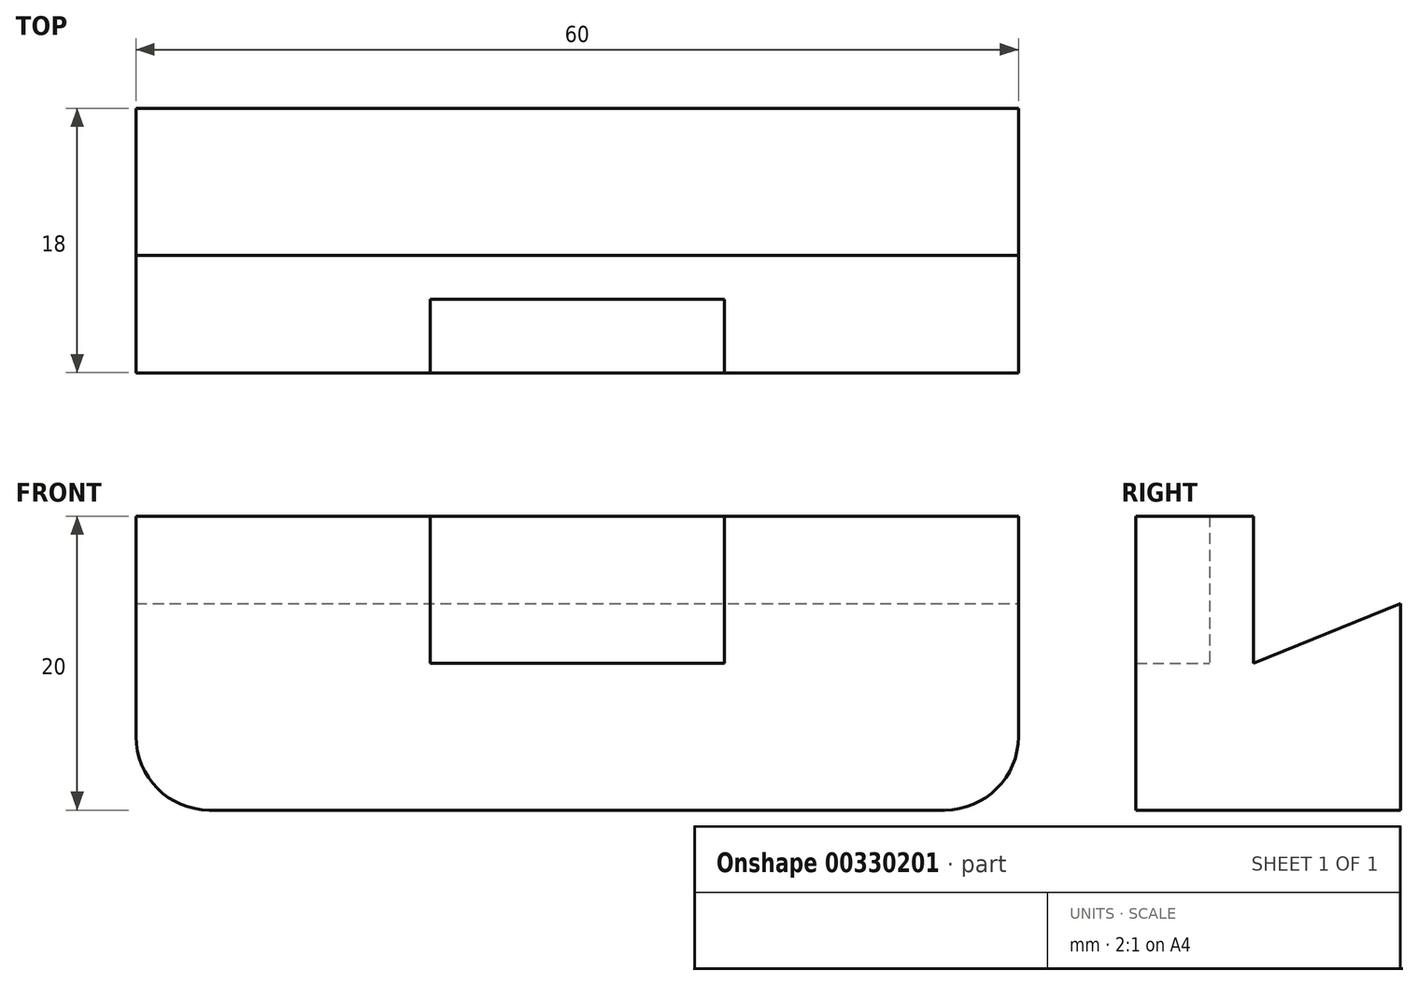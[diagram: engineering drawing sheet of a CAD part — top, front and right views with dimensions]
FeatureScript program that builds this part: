
annotation { "Feature Type Name" : "Feature", "Feature Type Description" : "" }
export const myFeature = defineFeature(function(context is Context, id is Id, definition is map)
    precondition{}
    {
        {
            var Q0;
            Q0=qCreatedBy(makeId("Top.planeOp"),FACE);
            var sketch = newSketch(context, id + "F0", { "sketchPlane" : qUnion([Q0])});
            skLineSegment(sketch, "E0.top", {"start": v(17.49, -21.5) * mm, "end": v(37.49, -21.5) * mm});
            skLineSegment(sketch, "E0.right", {"start": v(37.49, -13.5) * mm, "end": v(37.49, -21.5) * mm});
            skLineSegment(sketch, "E1", {"start": v(17.49, -16.5) * mm, "end": v(17.49, -21.5) * mm});
            skLineSegment(sketch, "E2.MirrorCS", {"start": v(-2.51, -16.5) * mm, "end": v(-2.51, -21.5) * mm});
            skLineSegment(sketch, "E3.MirrorCS", {"start": v(-2.51, -21.5) * mm, "end": v(-22.51, -21.5) * mm});
            skLineSegment(sketch, "E4.MirrorCS", {"start": v(-22.51, -13.5) * mm, "end": v(-22.51, -21.5) * mm});
            skLineSegment(sketch, "E5", {"start": v(-2.51, -16.5) * mm, "end": v(17.49, -16.5) * mm});
            skLineSegment(sketch, "E6", {"start": v(37.49, -13.5) * mm, "end": v(-22.51, -13.5) * mm});
            skPoint(sketch, "E7.startSnap0", {"position": v(7.49, -16.5) * mm});
            skPoint(sketch, "E7.endSnap0", {"position": v(7.49, -13.5) * mm});
            skSolve(sketch);
        }
        {
            var Q0;
            Q0=qSketchRegion(id+"F0",true);
            extrude(context, id + "F1", {"entities" : qUnion([Q0]), "depth" : 20 * mm});
        }
        {
            var Q0;
            Q0=makeQuery(id+"F1.opExtrude","CAP_EDGE",EDGE,{"disambiguationData":[OSD([sQuery(id+"F0.wireOp",EDGE,"E4.MirrorCS")])],"isStart":true});
            var Q1;
            Q1=makeQuery(id+"F1.opExtrude","CAP_EDGE",EDGE,{"disambiguationData":[OSD([sQuery(id+"F0.wireOp",EDGE,"E0.right")])],"isStart":true});
            fillet(context, id + "F2", {"entities" : qUnion([Q0, Q1]), "radius" : 5 * mm, "tangentPropagation" : true, "allowEdgeOverflow" : false});
        }
        {
            var Q0;
            Q0=makeQuery(id+"F1.opExtrude","SWEPT_FACE",FACE,{"disambiguationData":[OSD([sQuery(id+"F0.wireOp",EDGE,"E5")])]});
            var sketch = newSketch(context, id + "F3", { "sketchPlane" : qUnion([Q0])});
            skLineSegment(sketch, "E8.bottom", {"start": v(-2.51, 10) * mm, "end": v(17.49, 10) * mm});
            skLineSegment(sketch, "E8.top", {"start": v(-2.51, 0) * mm, "end": v(17.49, 0) * mm});
            skLineSegment(sketch, "E8.left", {"start": v(-2.51, 10) * mm, "end": v(-2.51, 0) * mm});
            skLineSegment(sketch, "E8.right", {"start": v(17.49, 10) * mm, "end": v(17.49, 0) * mm});
            skSolve(sketch);
        }
        {
            var Q0;
            Q0=makeQuery(id+"F3.imprint","IMPRINT",FACE,{"disambiguationData":[TD([[makeQuery(id+"F3.imprint","IMPRINT",EDGE,{"derivedFrom":sQuery(id+"F3.wireOp",EDGE,"E8.bottom")}),-1.0]])]});
            var Q1;
            Q1 = qSketchRegion(id + "F3", true);
            extrude(context, id + "F4", {"entities" : qUnion([Q0, Q1]), "operationType" : NewBodyOperationType.ADD, "depth" : 5 * mm});
        }
        {
            var Q0;
            Q0=makeQuery(id+"F1.opExtrude","SWEPT_FACE",FACE,{"disambiguationData":[OSD([sQuery(id+"F0.wireOp",EDGE,"E6")])]});
            extrude(context, id + "F5", {"entities" : qUnion([Q0]), "operationType" : NewBodyOperationType.ADD, "depth" : 10 * mm});
        }
        {
            var Q0;
            {var subQ0=sQuery(id+"F0.wireOp",EDGE,"E6");var subQ1=sQuery(id+"F0.wireOp",EDGE,"E0.right");Q0=makeQuery(id+"F5.boolean.opBoolean","MERGE",FACE,{"derivedFrom":[makeQuery(id+"F1.opExtrude","SWEPT_FACE",FACE,{"disambiguationData":[OSD([subQ1])]}),makeQuery(id+"F5.opExtrude","SWEPT_FACE",FACE,{"disambiguationData":[OSD([subQ1,subQ0]),TDD([makeQuery(id+"F1.opExtrude","SWEPT_EDGE",EDGE,{"disambiguationData":[OSD([subQ1,subQ0])]})])]})]});}
            var sketch = newSketch(context, id + "F6", { "sketchPlane" : qUnion([Q0])});
            skLineSegment(sketch, "E9.bottom", {"start": v(-3.5, 20) * mm, "end": v(-13.5, 20) * mm});
            skLineSegment(sketch, "E9.top", {"start": v(-3.5, 14.04) * mm, "end": v(-13.5, 10) * mm});
            skLineSegment(sketch, "E9.left", {"start": v(-3.5, 20) * mm, "end": v(-3.5, 14.04) * mm});
            skLineSegment(sketch, "E9.right", {"start": v(-13.5, 20) * mm, "end": v(-13.5, 10) * mm});
            skSolve(sketch);
        }
        {
            var Q0;
            Q0=makeQuery(id+"F6.imprint","IMPRINT",FACE,{"disambiguationData":[TD([[makeQuery(id+"F6.imprint","IMPRINT",EDGE,{"derivedFrom":sQuery(id+"F6.wireOp",EDGE,"E9.bottom")}),1.0]])]});
            extrude(context, id + "F7", {"entities" : qUnion([Q0]), "operationType" : NewBodyOperationType.REMOVE, "endBound" : BoundingType.THROUGH_ALL, "oppositeDirection" : true, "depth" : 25 * mm});
        }
    });
